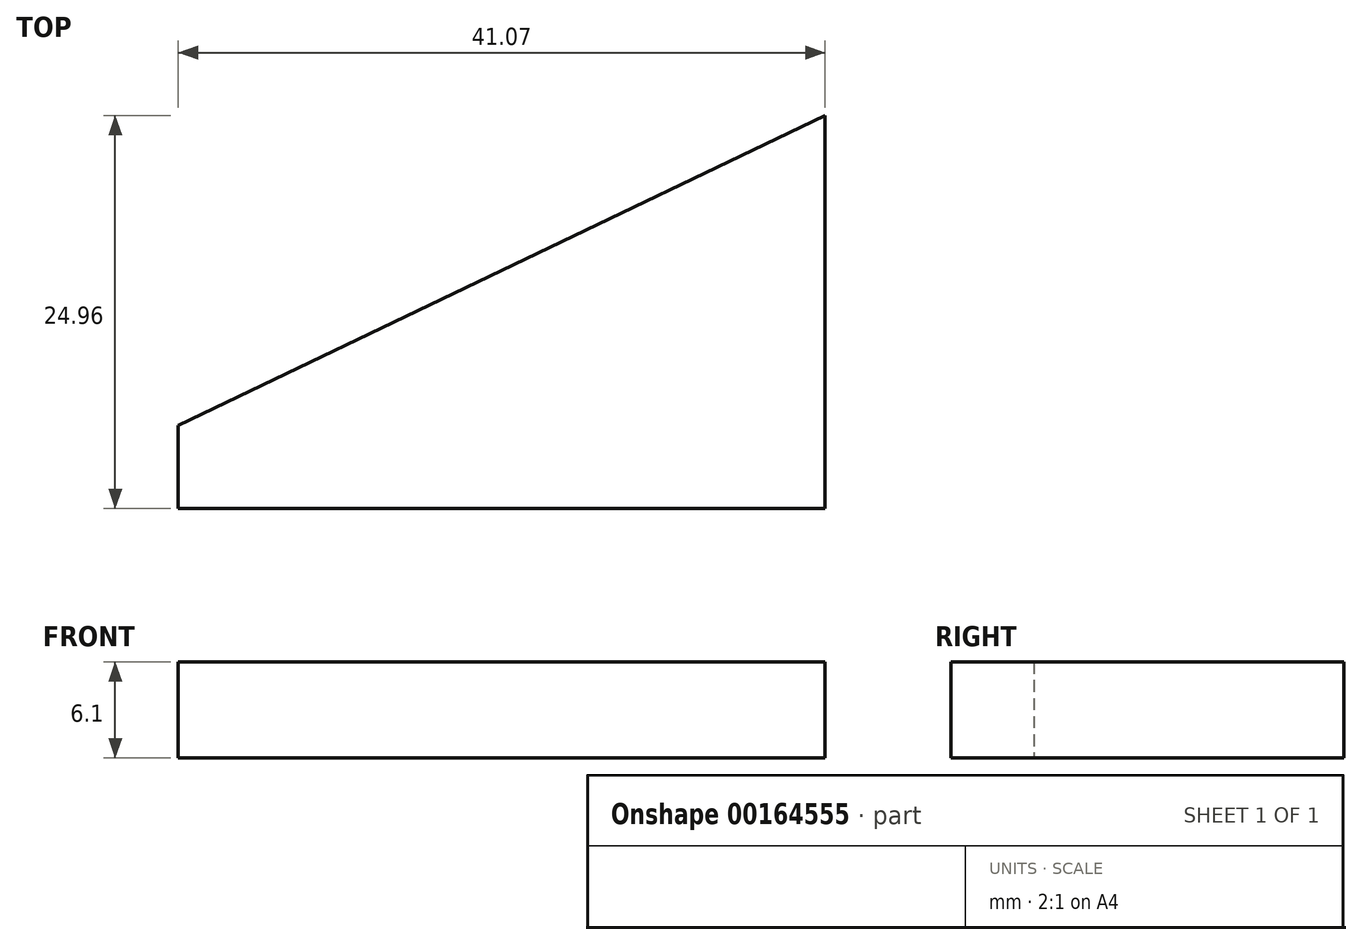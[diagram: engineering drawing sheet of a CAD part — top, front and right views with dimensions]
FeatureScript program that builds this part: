
annotation { "Feature Type Name" : "Feature", "Feature Type Description" : "" }
export const myFeature = defineFeature(function(context is Context, id is Id, definition is map)
    precondition{}
    {
        {
            var Q0;
            Q0=qCreatedBy(makeId("Top.planeOp"),FACE);
            var sketch = newSketch(context, id + "F0", { "sketchPlane" : qUnion([Q0])});
            skLineSegment(sketch, "E0", {"start": v(0, 0) * mm, "end": v(-41.07, 0) * mm});
            skLineSegment(sketch, "E1", {"start": v(-41.07, 0) * mm, "end": v(-41.07, 5.28) * mm});
            skLineSegment(sketch, "E2", {"start": v(-41.07, 5.28) * mm, "end": v(0, 24.96) * mm});
            skLineSegment(sketch, "E3", {"start": v(0, 24.96) * mm, "end": v(0, 0) * mm});
            skSolve(sketch);
        }
        {
            var Q0;
            Q0=makeQuery(id+"F0.imprint","IMPRINT",FACE,{"disambiguationData":[TD([[makeQuery(id+"F0.imprint","IMPRINT",EDGE,{"derivedFrom":sQuery(id+"F0.wireOp",EDGE,"E0")}),-1.0]])]});
            extrude(context, id + "F1", {"entities" : qUnion([Q0]), "depth" : 6.1 * mm});
        }
    });
